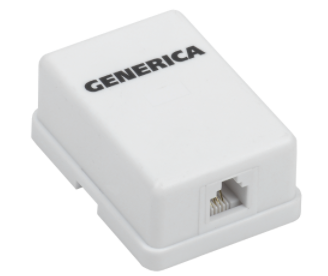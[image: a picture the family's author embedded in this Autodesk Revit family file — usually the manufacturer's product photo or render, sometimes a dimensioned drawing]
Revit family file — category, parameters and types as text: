
# Revit family: ITK_Розетка информационная GENERICA_Настенная_1 порт_IP20
name_source: partatom
category: Обобщенные модели
units: mm (PartAtom-declared; Revit-internal decimal feet)

## family parameters
Всегда вертикально = Да
Может служить основой для арматурных стержней = Нет
На основе рабочей плоскости = Нет
Общий = Нет
При загрузке вырезать с полостями = Нет
Размер круглого соединителя = Использовать диаметр
Тип детали = Нормальный
Точка расчета площади = Нет

## types (2) — shared parameters
ADSK_URL страницы изделия = https://generica.su
ADSK_Версия Revit = 2019
ADSK_Версия семейства = 1.0
ADSK_Группирование = I. ЩИТЫ И ПУЛЬТЫ
ADSK_Единица измерения = шт
ADSK_Завод-изготовитель = IEK
ADSK_Материал наименование = АБС-пластик
IEK_URL = https://generica.su
IEK_Описание = Используется для подключения оконечного оборудования пользователей на рабочих местах к информационной сети.
KSI_CMa_Строительные материалы = 01.7.14.03
URL = https://www.iek.ru
Высота = 24 мм
Глубина = 58 мм
Изготовитель = ITK
Материал = Пластик белый
Степень защиты = IP20
Ширина = 47 мм
zero-valued in all types: ADSK_Масса

## per-type parameters (varying)
| type | ADSK_Код изделия | ADSK_Наименование | IEK_Цена за единицу |
| Категория 5E_UTP | CS2-1C5EU-12-G | Розетка инф. настенная RJ45 кат. 5Е UTP 1 порт GENERICA | 128.94 |
| Категория 5E_FTP | CS2-1C5EF-12-G | Розетка инф. настенная RJ45 кат. 5Е FTP 1 порт GENERICA | 165.1 |
